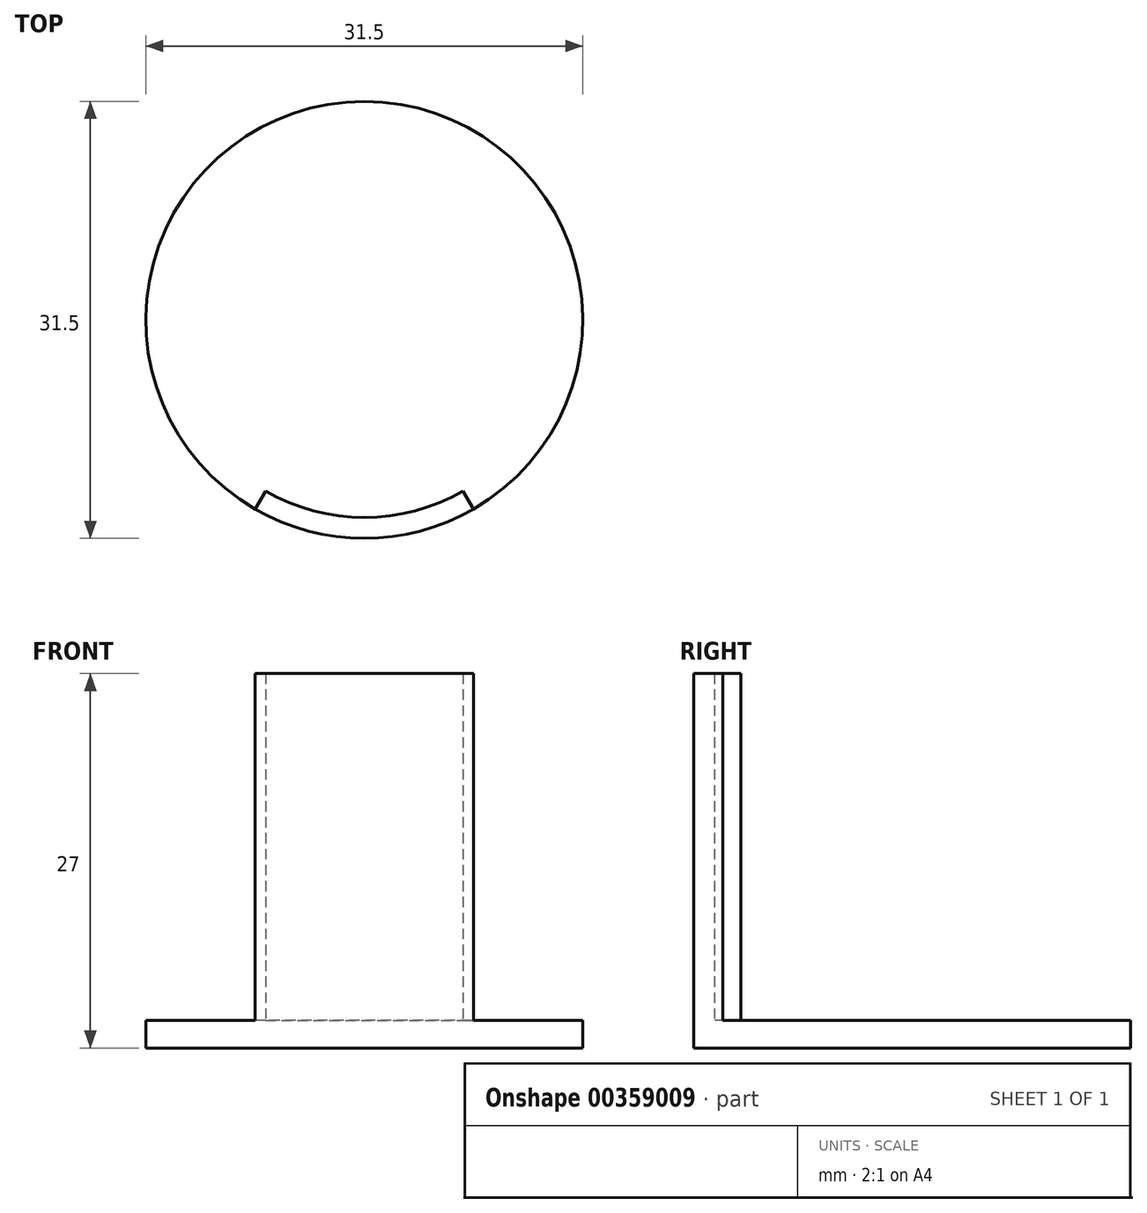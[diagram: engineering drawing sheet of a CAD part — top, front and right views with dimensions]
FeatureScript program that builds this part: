
annotation { "Feature Type Name" : "Feature", "Feature Type Description" : "" }
export const myFeature = defineFeature(function(context is Context, id is Id, definition is map)
    precondition{}
    {
        {
            var Q0;
            Q0=qCreatedBy(makeId("Top.planeOp"),FACE);
            var sketch = newSketch(context, id + "F0", { "sketchPlane" : qUnion([Q0])});
            skCircle(sketch, "E0", {"center": v(0, 0) * mm, "radius": 15.75 * mm});
            skSolve(sketch);
        }
        {
            var Q0;
            Q0 = qSketchRegion(id + "F0", true);
            extrude(context, id + "F1", {"entities" : qUnion([Q0]), "depth" : 2 * mm});
        }
        {
            var Q0;
            Q0=makeQuery(id+"F1.opExtrude","CAP_FACE",FACE,{"disambiguationData":[OSD([sQuery(id+"F0.wireOp",EDGE,"E0")])],"isStart":false});
            var sketch = newSketch(context, id + "F2", { "sketchPlane" : qUnion([Q0])});
            skArc(sketch, "E1", {"start": v(-7.88, -13.64) * mm, "mid": v(0, -15.75) * mm, "end": v(7.88, -13.64) * mm});
            skArc(sketch, "E2.0", {"start": v(-7.13, -12.34) * mm, "mid": v(0, -14.25) * mm, "end": v(7.13, -12.34) * mm});
            skLineSegment(sketch, "E3", {"start": v(-7.13, -12.34) * mm, "end": v(-7.88, -13.64) * mm});
            skLineSegment(sketch, "E4", {"start": v(7.13, -12.34) * mm, "end": v(7.88, -13.64) * mm});
            skSolve(sketch);
        }
        {
            var Q0;
            Q0 = qSketchRegion(id + "F2", true);
            extrude(context, id + "F3", {"entities" : qUnion([Q0]), "operationType" : NewBodyOperationType.ADD, "depth" : 25 * mm});
        }
    });
